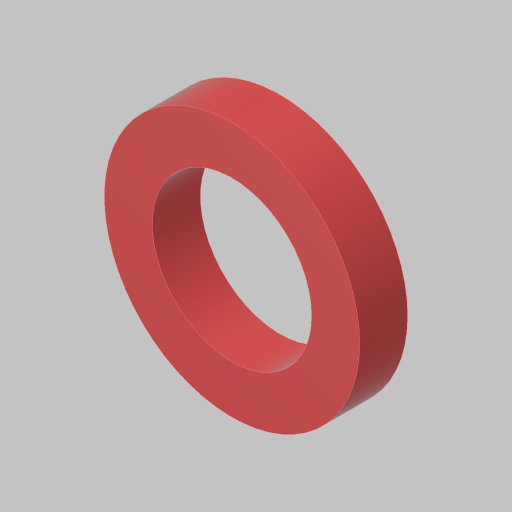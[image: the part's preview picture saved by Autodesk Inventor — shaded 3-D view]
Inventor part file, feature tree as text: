
AUTODESK INVENTOR PART (.ipt)
format: ipt  version: 2023.5 (Build 275446000, 446)  size: 104,448 bytes
history: native  units: in
note: dims shown in document units (in); Inventor stores cm internally (conversion verified against a paired STEP export)
features: extrude x1, sketch x1
ambient origin geometry x8: Origin, YZ Plane, XZ Plane, XY Plane, X Axis, Y Axis, Z Axis, Center Point
bodies: Solid1 (feature_tree)
feature tree (2):
  extrude  "Extrusion1"  Depth=0.125in
  sketch  "Sketch1"  dims[d0=0.125in d1=0.415in d2=0.125in d3=0.0in]
